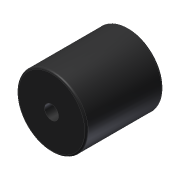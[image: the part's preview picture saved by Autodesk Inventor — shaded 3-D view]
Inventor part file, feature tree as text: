
AUTODESK INVENTOR PART (.ipt)
format: ipt  version: 2012 (Build 160160000, 160)  size: 93,696 bytes
history: native  units: in
note: dims shown in document units (in); Inventor stores cm internally (conversion verified against a paired STEP export)
features: extrude x1, fillet x1, sketch x1
ambient origin geometry x8: Origin, YZ Plane, XZ Plane, XY Plane, X Axis, Y Axis, Z Axis, Center Point
bodies: Solid1 (feature_tree)
feature tree (3):
  extrude  "Extrusion1"  Depth=0.25in
  fillet  "Fillet1"  Radius=1.375in
  sketch  "Sketch1"  dims[d0=1.25in d1=0.25in d2=1.375in d3=0.0in d4=0.0312in]
